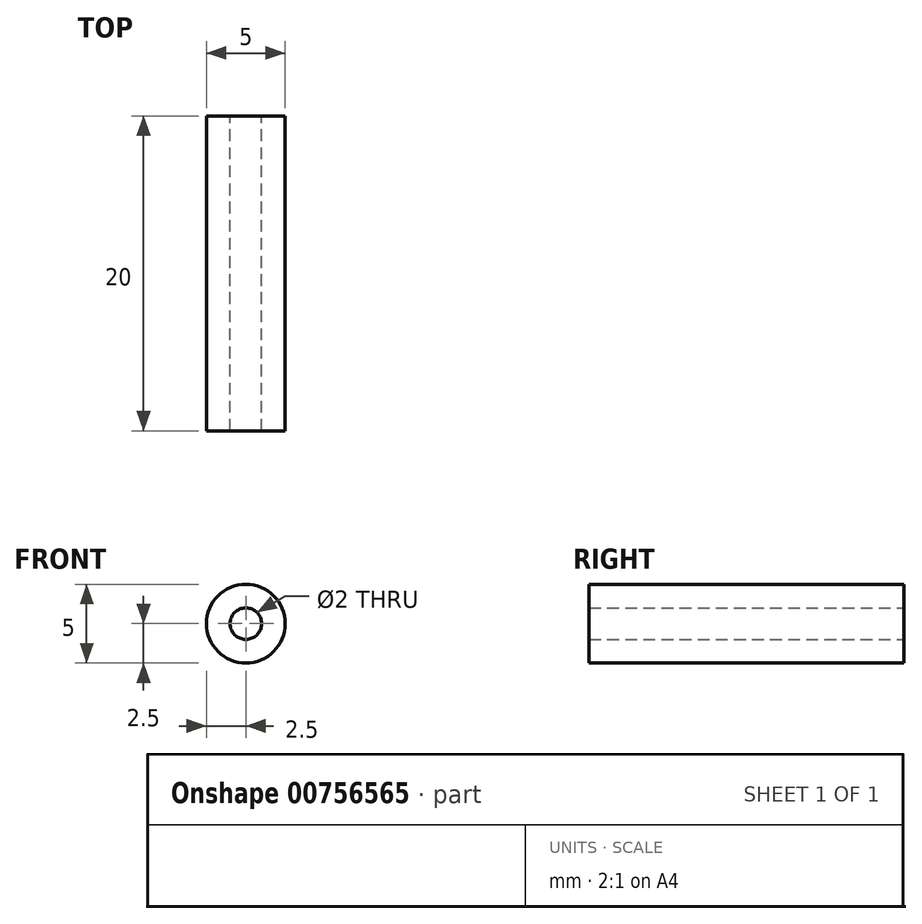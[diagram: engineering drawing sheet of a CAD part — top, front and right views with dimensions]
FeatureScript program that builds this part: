
annotation { "Feature Type Name" : "Feature", "Feature Type Description" : "" }
export const myFeature = defineFeature(function(context is Context, id is Id, definition is map)
    precondition{}
    {
        {
            var Q0;
            Q0=qCreatedBy(makeId("Front.planeOp"),FACE);
            var sketch = newSketch(context, id + "F0", { "sketchPlane" : qUnion([Q0])});
            skCircle(sketch, "E0", {"center": v(0, 0) * mm, "radius": 2.5 * mm});
            skSolve(sketch);
        }
        {
            var Q0;
            Q0 = qSketchRegion(id + "F0", true);
            var Q1;
            Q1=sQuery(id+"F0.wireOp",EDGE,"E0");
            extrude(context, id + "F1", {"entities" : qUnion([Q0]), "surfaceEntities" : qUnion([Q1]), "depth" : 20 * mm, "offsetDistance" : 25 * mm});
        }
        {
            var Q0;
            Q0=sQuery(id+"F0.wireOp",VERTEX,"E0.center");
            var Q1;
            Q1=makeQuery(id+"F1.opExtrude","SWEPT_BODY",BODY,{"disambiguationData":[OSD([sQuery(id+"F0.wireOp",EDGE,"E0")])]});
            hole(context, id + "F2", {"style" : HoleStyle.SIMPLE, "endStyle" : HoleEndStyle.THROUGH, "oppositeDirection" : true, "holeDiameter" : 2 * mm, "majorDiameter" : 5 * mm, "isTappedThrough" : true, "tappedDepth" : 12 * mm, "tapClearance" : 3, "locations" : qUnion([Q0]), "scope" : qUnion([Q1])});
        }
    });
